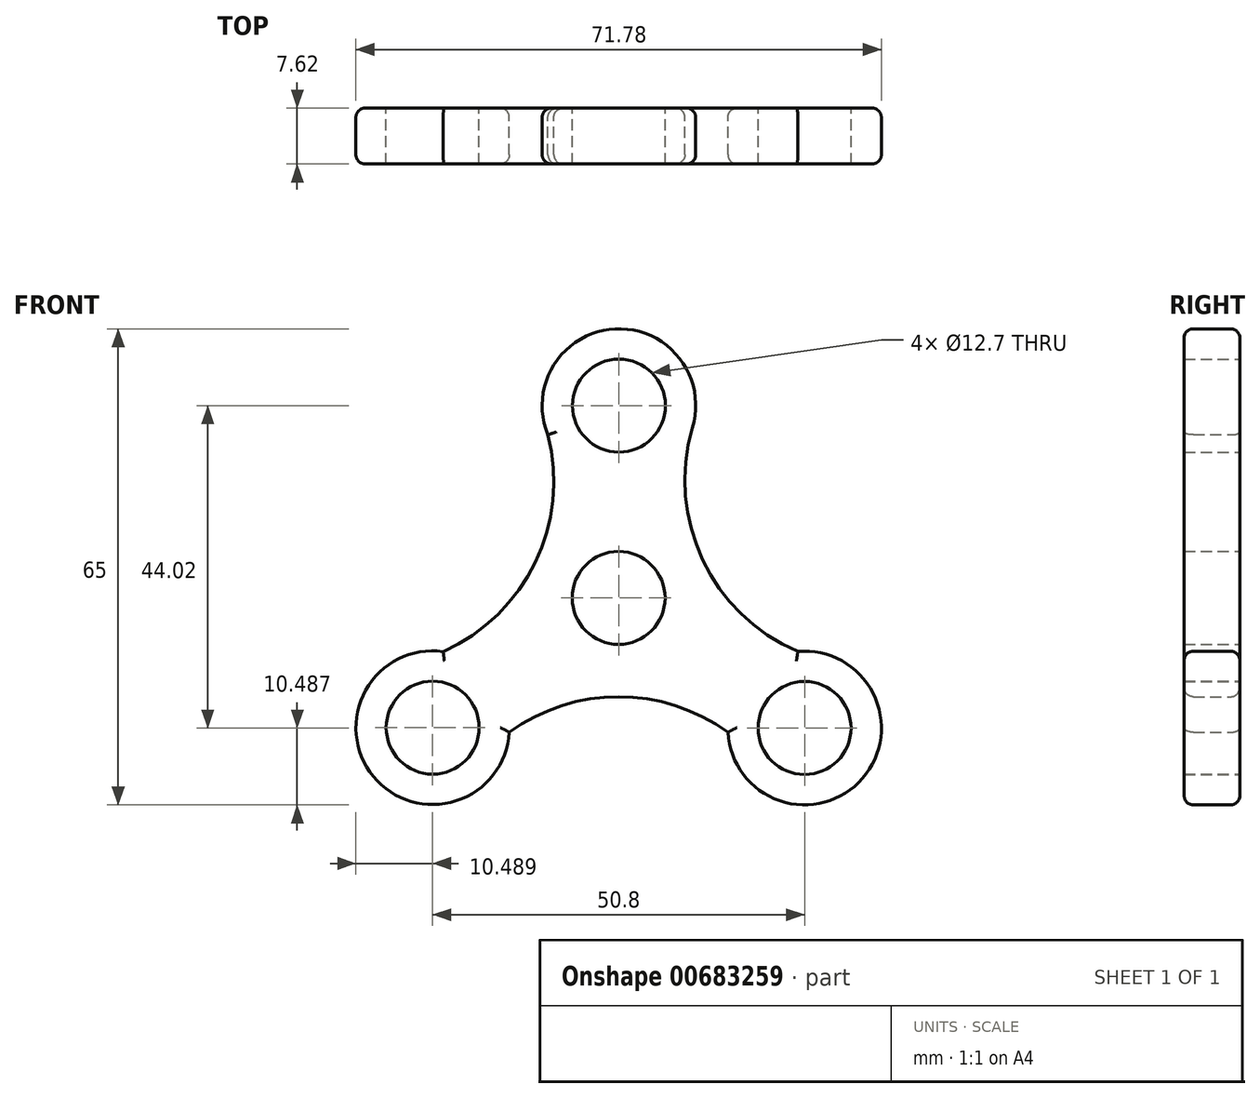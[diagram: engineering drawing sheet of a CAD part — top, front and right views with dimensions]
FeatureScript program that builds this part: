
annotation { "Feature Type Name" : "Feature", "Feature Type Description" : "" }
export const myFeature = defineFeature(function(context is Context, id is Id, definition is map)
    precondition{}
    {
        {
            var Q0;
            Q0=qCreatedBy(makeId("Front.planeOp"),FACE);
            var sketch = newSketch(context, id + "F0", { "sketchPlane" : qUnion([Q0])});
            skCircle(sketch, "E0", {"center": v(-5.37, 44.6) * mm, "radius": 10.5 * mm});
            skCircle(sketch, "E1", {"center": v(-30.81, 0.63) * mm, "radius": 10.5 * mm});
            skCircle(sketch, "E2", {"center": v(19.99, 0.58) * mm, "radius": 10.5 * mm});
            skCircle(sketch, "E3", {"center": v(-5.41, 18.33) * mm, "radius": 6.35 * mm});
            skArc(sketch, "E4", {"start": v(-29.39, 11.02) * mm, "mid": v(-16.8, 23.2) * mm, "end": v(-15.07, 40.62) * mm});
            skArc(sketch, "E5", {"start": v(4.67, 41.56) * mm, "mid": v(6.07, 23.56) * mm, "end": v(19.08, 11.03) * mm});
            skArc(sketch, "E6", {"start": v(9.51, 0) * mm, "mid": v(-5.41, 4.85) * mm, "end": v(-20.34, 0) * mm});
            skCircle(sketch, "E7", {"center": v(-5.37, 44.6) * mm, "radius": 6.35 * mm});
            skCircle(sketch, "E8", {"center": v(19.99, 0.58) * mm, "radius": 6.35 * mm});
            skCircle(sketch, "E9", {"center": v(-30.81, 0.63) * mm, "radius": 6.35 * mm});
            skSolve(sketch);
        }
        {
            var Q0;
            Q0=makeQuery(id+"F0.imprint","IMPRINT",FACE,{"disambiguationData":[TD([[makeQuery(id+"F0.imprint","IMPRINT",EDGE,{"derivedFrom":sQuery(id+"F0.wireOp",EDGE,"E3")}),-1.0]])]});
            var Q1;
            Q1=makeQuery(id+"F0.imprint","IMPRINT",FACE,{"disambiguationData":[TD([[makeQuery(id+"F0.imprint","IMPRINT",EDGE,{"derivedFrom":sQuery(id+"F0.wireOp",EDGE,"E9")}),-1.0]])]});
            var Q2;
            Q2=makeQuery(id+"F0.imprint","IMPRINT",FACE,{"disambiguationData":[TD([[makeQuery(id+"F0.imprint","IMPRINT",EDGE,{"derivedFrom":sQuery(id+"F0.wireOp",EDGE,"E8")}),-1.0]])]});
            var Q3;
            Q3=makeQuery(id+"F0.imprint","IMPRINT",FACE,{"disambiguationData":[TD([[makeQuery(id+"F0.imprint","IMPRINT",EDGE,{"derivedFrom":sQuery(id+"F0.wireOp",EDGE,"E7")}),-1.0]])]});
            extrude(context, id + "F1", {"entities" : qUnion([Q0, Q1, Q2, Q3]), "depth" : 7.62 * mm, "offsetDistance" : 25.4 * mm});
        }
        {
            var Q0;
            Q0=makeQuery(id+"F1.opExtrude","CAP_EDGE",EDGE,{"disambiguationData":[OSD([sQuery(id+"F0.wireOp",EDGE,"E5")])],"isStart":true});
            var Q1;
            Q1=makeQuery(id+"F1.opExtrude","CAP_EDGE",EDGE,{"disambiguationData":[OSD([sQuery(id+"F0.wireOp",EDGE,"E2")])],"isStart":true});
            var Q2;
            Q2=makeQuery(id+"F1.opExtrude","CAP_EDGE",EDGE,{"disambiguationData":[OSD([sQuery(id+"F0.wireOp",EDGE,"E6")])],"isStart":true});
            var Q3;
            Q3=makeQuery(id+"F1.opExtrude","CAP_EDGE",EDGE,{"disambiguationData":[OSD([sQuery(id+"F0.wireOp",EDGE,"E4")])],"isStart":true});
            var Q4;
            Q4=makeQuery(id+"F1.opExtrude","CAP_EDGE",EDGE,{"disambiguationData":[OSD([sQuery(id+"F0.wireOp",EDGE,"E1")])],"isStart":true});
            var Q5;
            Q5=makeQuery(id+"F1.opExtrude","CAP_EDGE",EDGE,{"disambiguationData":[OSD([sQuery(id+"F0.wireOp",EDGE,"E0")])],"isStart":true});
            var Q6;
            Q6=makeQuery(id+"F1.opExtrude","CAP_EDGE",EDGE,{"disambiguationData":[OSD([sQuery(id+"F0.wireOp",EDGE,"E0")])],"isStart":false});
            var Q7;
            Q7=makeQuery(id+"F1.opExtrude","CAP_EDGE",EDGE,{"disambiguationData":[OSD([sQuery(id+"F0.wireOp",EDGE,"E5")])],"isStart":false});
            var Q8;
            Q8=makeQuery(id+"F1.opExtrude","CAP_EDGE",EDGE,{"disambiguationData":[OSD([sQuery(id+"F0.wireOp",EDGE,"E4")])],"isStart":false});
            var Q9;
            Q9=makeQuery(id+"F1.opExtrude","CAP_EDGE",EDGE,{"disambiguationData":[OSD([sQuery(id+"F0.wireOp",EDGE,"E1")])],"isStart":false});
            var Q10;
            Q10=makeQuery(id+"F1.opExtrude","CAP_EDGE",EDGE,{"disambiguationData":[OSD([sQuery(id+"F0.wireOp",EDGE,"E6")])],"isStart":false});
            var Q11;
            Q11=makeQuery(id+"F1.opExtrude","CAP_EDGE",EDGE,{"disambiguationData":[OSD([sQuery(id+"F0.wireOp",EDGE,"E2")])],"isStart":false});
            fillet(context, id + "F2", {"entities" : qUnion([Q0, Q1, Q2, Q3, Q4, Q5, Q6, Q7, Q8, Q9, Q10, Q11]), "radius" : 1.27 * mm, "tangentPropagation" : true, "allowEdgeOverflow" : false});
        }
    });
